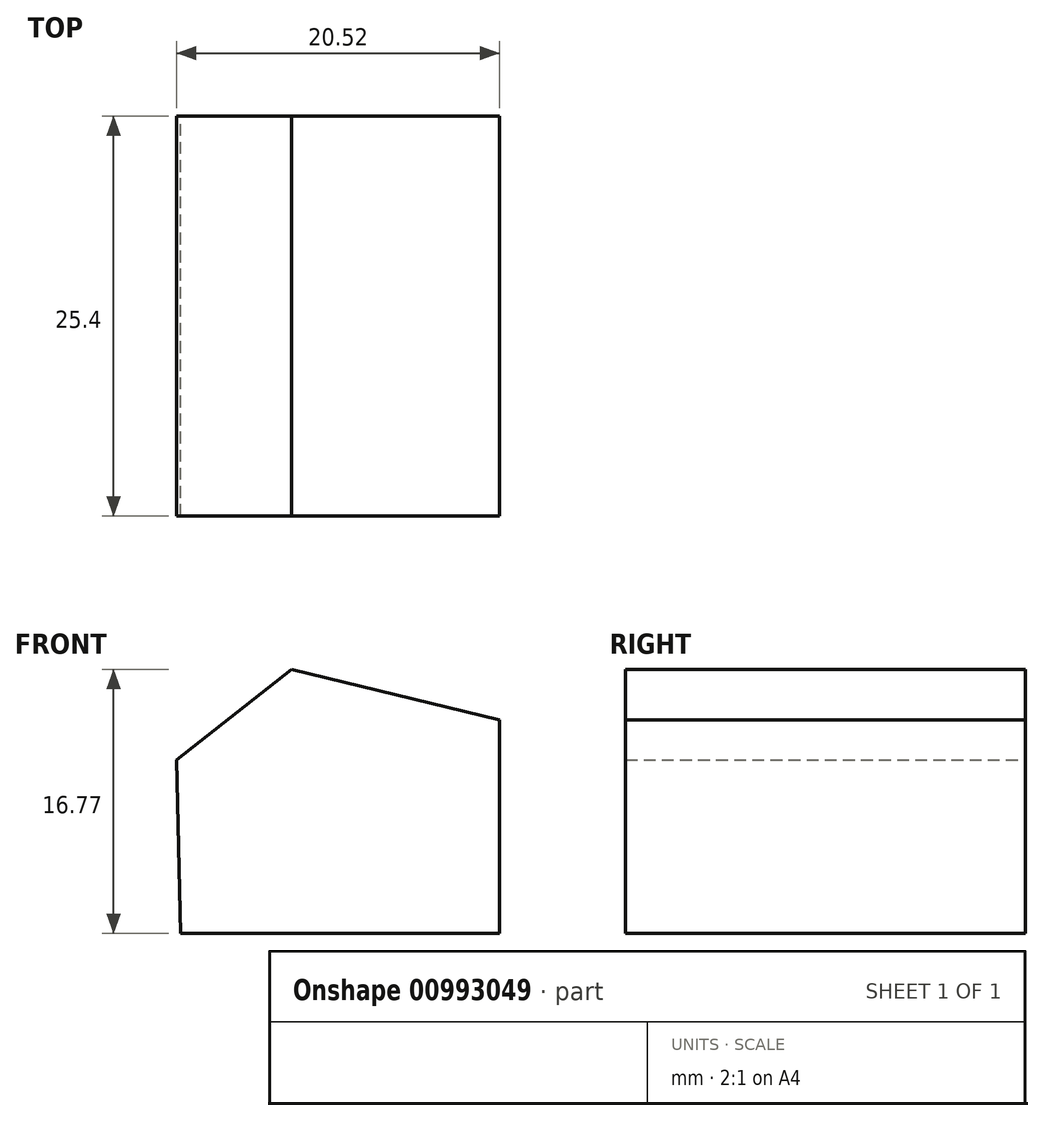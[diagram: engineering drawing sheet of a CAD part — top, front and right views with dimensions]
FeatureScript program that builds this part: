
annotation { "Feature Type Name" : "Feature", "Feature Type Description" : "" }
export const myFeature = defineFeature(function(context is Context, id is Id, definition is map)
    precondition{}
    {
        {
            var Q0;
            Q0=qCreatedBy(makeId("Front.planeOp"),FACE);
            var sketch = newSketch(context, id + "F0", { "sketchPlane" : qUnion([Q0])});
            skLineSegment(sketch, "E0", {"start": v(-15, 5.03) * mm, "end": v(-7.72, 10.77) * mm});
            skLineSegment(sketch, "E1", {"start": v(-7.72, 10.77) * mm, "end": v(5.5, 7.55) * mm});
            skLineSegment(sketch, "E2", {"start": v(5.5, 7.55) * mm, "end": v(5.5, -6) * mm});
            skLineSegment(sketch, "E3", {"start": v(5.5, -6) * mm, "end": v(-14.75, -6) * mm});
            skLineSegment(sketch, "E4", {"start": v(-14.75, -6) * mm, "end": v(-15, 5.03) * mm});
            skSolve(sketch);
        }
        {
            var Q0;
            Q0=makeQuery(id+"F0.imprint","IMPRINT",FACE,{"disambiguationData":[TD([[makeQuery(id+"F0.imprint","IMPRINT",EDGE,{"derivedFrom":sQuery(id+"F0.wireOp",EDGE,"E0")}),-1.0]])]});
            extrude(context, id + "F1", {"entities" : qUnion([Q0]), "depth" : 25.4 * mm, "offsetDistance" : 25.4 * mm});
        }
    });
